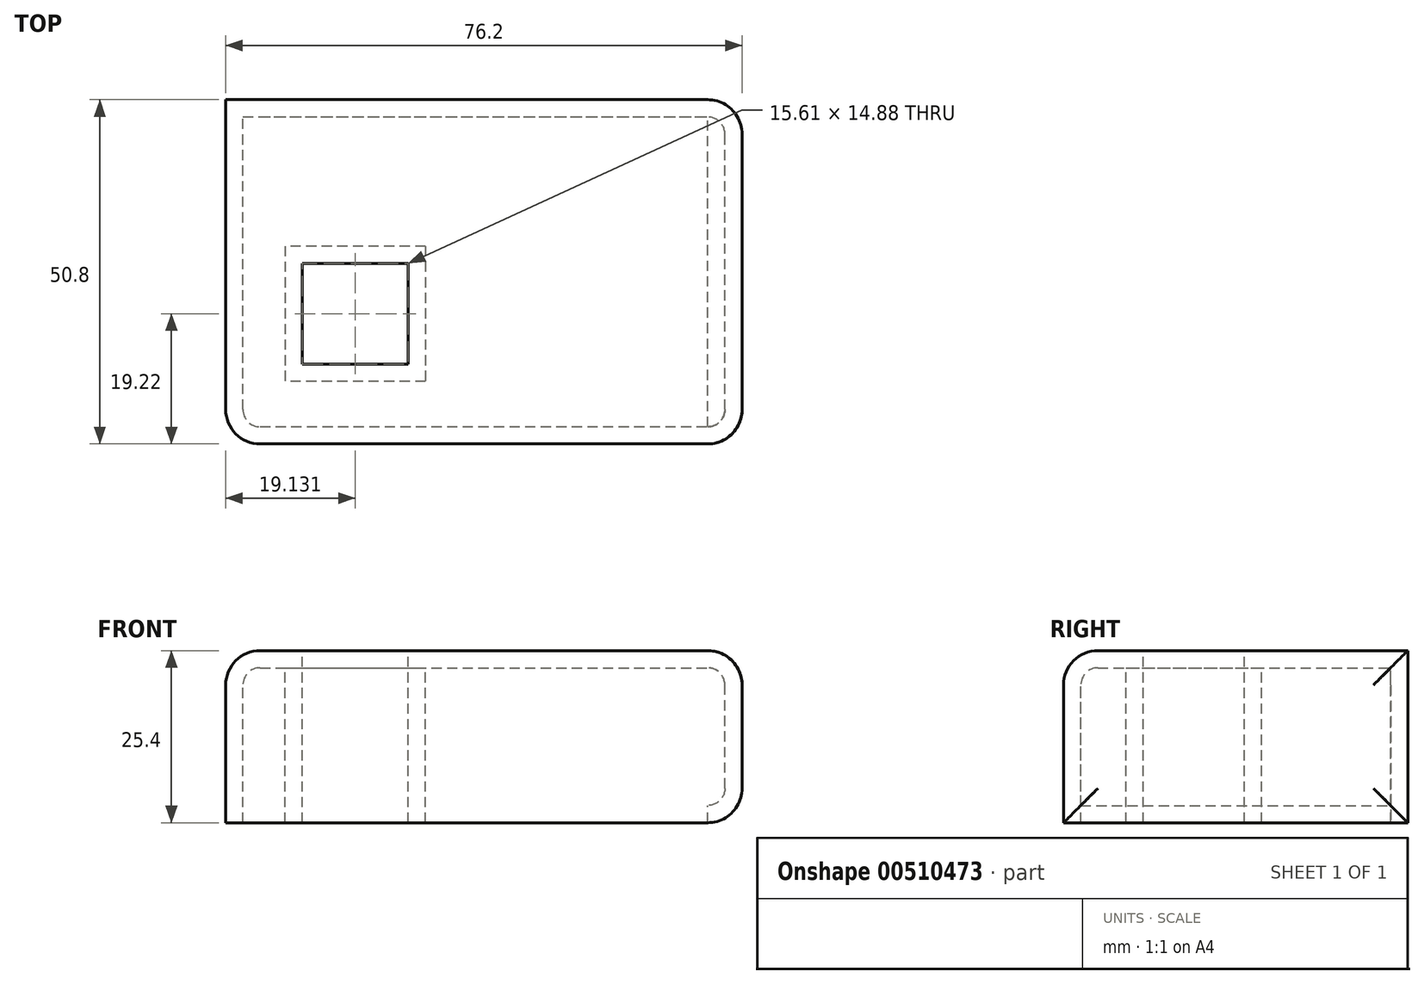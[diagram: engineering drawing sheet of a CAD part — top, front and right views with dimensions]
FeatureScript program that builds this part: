
annotation { "Feature Type Name" : "Feature", "Feature Type Description" : "" }
export const myFeature = defineFeature(function(context is Context, id is Id, definition is map)
    precondition{}
    {
        {
            var Q0;
            Q0=qCreatedBy(makeId("Top.planeOp"),FACE);
            var sketch = newSketch(context, id + "F0", { "sketchPlane" : qUnion([Q0])});
            skLineSegment(sketch, "E0.bottom", {"start": v(0, 0) * mm, "end": v(76.2, 0) * mm});
            skLineSegment(sketch, "E0.top", {"start": v(0, 50.8) * mm, "end": v(76.2, 50.8) * mm});
            skLineSegment(sketch, "E0.left", {"start": v(0, 0) * mm, "end": v(0, 50.8) * mm});
            skLineSegment(sketch, "E0.right", {"start": v(76.2, 0) * mm, "end": v(76.2, 50.8) * mm});
            skSolve(sketch);
        }
        {
            var Q0;
            Q0=makeQuery(id+"F0.imprint","IMPRINT",FACE,{"disambiguationData":[TD([[makeQuery(id+"F0.imprint","IMPRINT",EDGE,{"derivedFrom":sQuery(id+"F0.wireOp",EDGE,"E0.bottom")}),1.0]])]});
            extrude(context, id + "F1", {"entities" : qUnion([Q0]), "depth" : 25.4 * mm});
        }
        {
            var Q0;
            Q0=makeQuery(id+"F1.opExtrude","CAP_FACE",FACE,{"disambiguationData":[OSD([sQuery(id+"F0.wireOp",EDGE,"E0.bottom"),sQuery(id+"F0.wireOp",EDGE,"E0.top"),sQuery(id+"F0.wireOp",EDGE,"E0.left"),sQuery(id+"F0.wireOp",EDGE,"E0.right")])],"isStart":false});
            var sketch = newSketch(context, id + "F2", { "sketchPlane" : qUnion([Q0])});
            skLineSegment(sketch, "E1.bottom", {"start": v(11.33, 11.78) * mm, "end": v(26.94, 11.78) * mm});
            skLineSegment(sketch, "E1.top", {"start": v(11.33, 26.66) * mm, "end": v(26.94, 26.66) * mm});
            skLineSegment(sketch, "E1.left", {"start": v(11.33, 11.78) * mm, "end": v(11.33, 26.66) * mm});
            skLineSegment(sketch, "E1.right", {"start": v(26.94, 11.78) * mm, "end": v(26.94, 26.66) * mm});
            skSolve(sketch);
        }
        {
            var Q0;
            Q0=makeQuery(id+"F2.imprint","IMPRINT",FACE,{"disambiguationData":[TD([[makeQuery(id+"F2.imprint","IMPRINT",EDGE,{"derivedFrom":sQuery(id+"F2.wireOp",EDGE,"E1.bottom")}),1.0]])]});
            extrude(context, id + "F3", {"entities" : qUnion([Q0]), "operationType" : NewBodyOperationType.REMOVE, "endBound" : BoundingType.UP_TO_NEXT, "oppositeDirection" : true, "depth" : 25.4 * mm});
        }
        {
            var Q0;
            Q0=makeQuery(id+"F1.opExtrude","CAP_EDGE",EDGE,{"disambiguationData":[OSD([sQuery(id+"F0.wireOp",EDGE,"E0.bottom")])],"isStart":false});
            var Q1;
            Q1=makeQuery(id+"F1.opExtrude","SWEPT_FACE",FACE,{"disambiguationData":[OSD([sQuery(id+"F0.wireOp",EDGE,"E0.right")])]});
            var Q2;
            Q2=makeQuery(id+"F1.opExtrude","SWEPT_EDGE",EDGE,{"disambiguationData":[OSD([sQuery(id+"F0.wireOp",EDGE,"E0.bottom"),sQuery(id+"F0.wireOp",EDGE,"E0.left")])]});
            var Q3;
            Q3=makeQuery(id+"F1.opExtrude","CAP_EDGE",EDGE,{"disambiguationData":[OSD([sQuery(id+"F0.wireOp",EDGE,"E0.left")])],"isStart":false});
            fillet(context, id + "F4", {"entities" : qUnion([Q0, Q1, Q2, Q3]), "radius" : 5.08 * mm, "tangentPropagation" : true, "allowEdgeOverflow" : false});
        }
        {
            var Q0;
            Q0=makeQuery(id+"F1.opExtrude","CAP_FACE",FACE,{"disambiguationData":[OSD([sQuery(id+"F0.wireOp",EDGE,"E0.bottom"),sQuery(id+"F0.wireOp",EDGE,"E0.top"),sQuery(id+"F0.wireOp",EDGE,"E0.left"),sQuery(id+"F0.wireOp",EDGE,"E0.right")])],"isStart":true});
            shell(context, id + "F5", {"entities" : qUnion([Q0]), "thickness" : 2.54 * mm});
        }
    });
